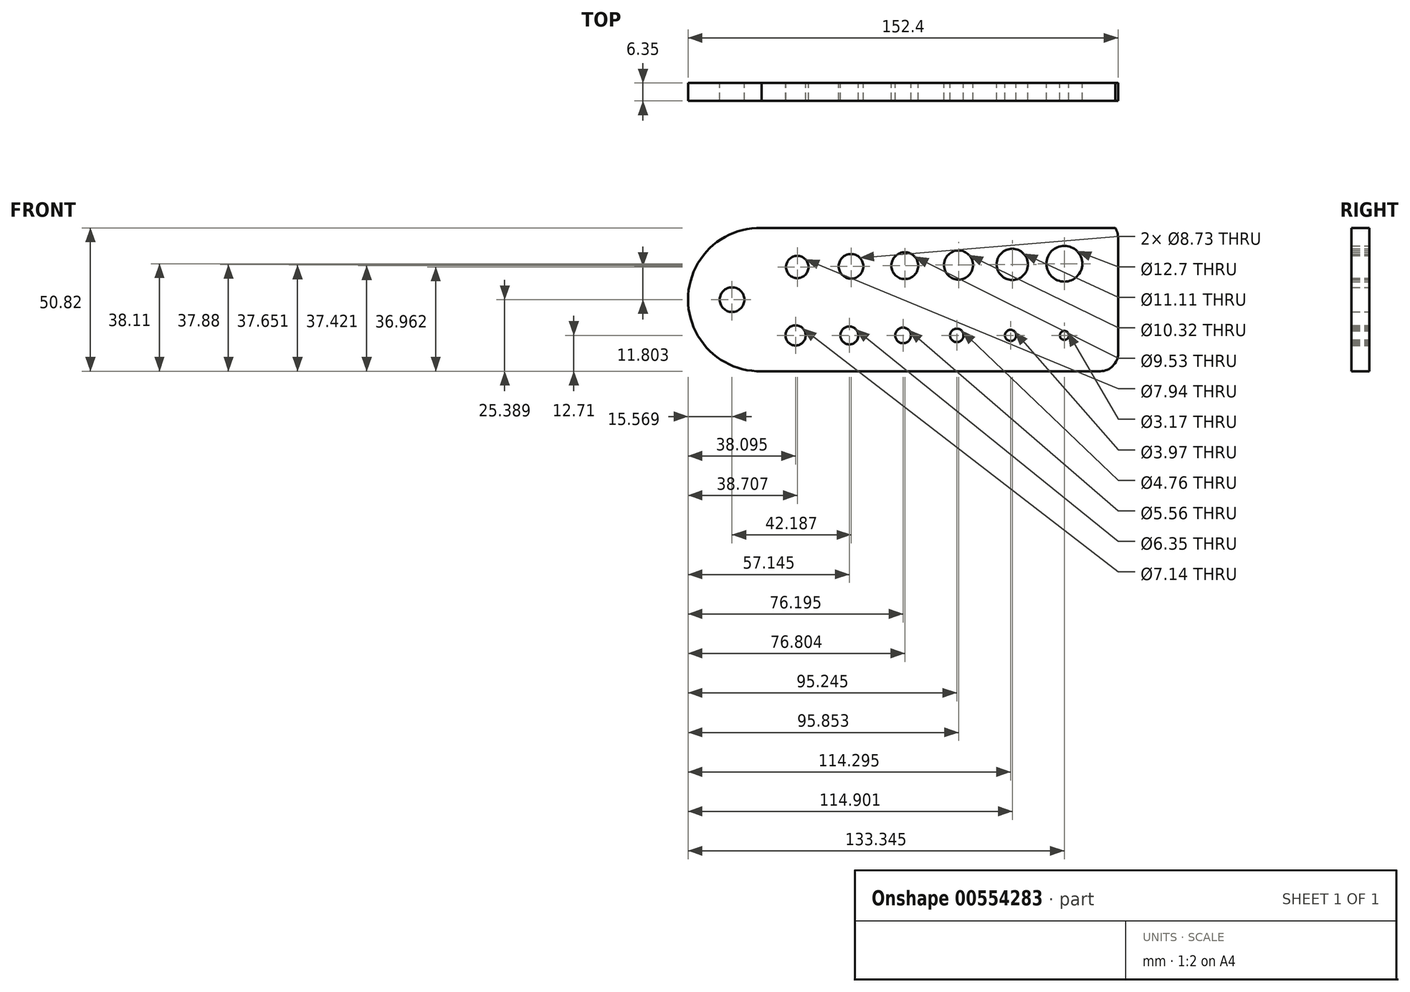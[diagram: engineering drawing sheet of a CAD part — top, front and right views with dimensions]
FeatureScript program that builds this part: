
annotation { "Feature Type Name" : "Feature", "Feature Type Description" : "" }
export const myFeature = defineFeature(function(context is Context, id is Id, definition is map)
    precondition{}
    {
        {
            var Q0;
            Q0=qCreatedBy(makeId("Front.planeOp"),FACE);
            var sketch = newSketch(context, id + "F0", { "sketchPlane" : qUnion([Q0])});
            skLineSegment(sketch, "E0.bottom", {"start": v(0, 0) * mm, "end": v(120.05, 0) * mm});
            skLineSegment(sketch, "E0.top", {"start": v(0, 50.8) * mm, "end": v(125.41, 50.8) * mm});
            skLineSegment(sketch, "E0.right", {"start": v(126.4, 6.35) * mm, "end": v(126.4, 47.4) * mm});
            skPoint(sketch, "E1.visualSharp", {"position": v(126.4, 50.8) * mm});
            skArc(sketch, "E1.filletArc", {"start": v(126.4, 47.4) * mm, "mid": v(126.14, 49.17) * mm, "end": v(125.41, 50.8) * mm});
            skPoint(sketch, "E2.visualSharp", {"position": v(126.4, 0) * mm});
            skArc(sketch, "E2.filletArc", {"start": v(120.05, 0) * mm, "mid": v(124.54, 1.86) * mm, "end": v(126.4, 6.35) * mm});
            skArc(sketch, "E3", {"start": v(0, 50.8) * mm, "mid": v(-26, 25.4) * mm, "end": v(0, 0) * mm});
            skCircle(sketch, "E4", {"center": v(107.35, 38.1) * mm, "radius": 6.35 * mm});
            skCircle(sketch, "E5.1.0.0", {"center": v(88.9, 37.87) * mm, "radius": 5.56 * mm});
            skCircle(sketch, "E5.2.0.0", {"center": v(69.85, 37.64) * mm, "radius": 5.16 * mm});
            skCircle(sketch, "E5.3.0.0", {"center": v(50.8, 37.41) * mm, "radius": 4.76 * mm});
            skCircle(sketch, "E5.4.0.0", {"center": v(31.76, 37.18) * mm, "radius": 4.37 * mm});
            skCircle(sketch, "E5.5.0.0", {"center": v(12.7, 36.95) * mm, "radius": 3.97 * mm});
            skLineSegment(sketch, "E5.direction1", {"start": v(107.95, 38.1) * mm, "end": v(88.9, 37.87) * mm, "construction": true});
            skCircle(sketch, "E6", {"center": v(107.35, 12.7) * mm, "radius": 1.59 * mm});
            skCircle(sketch, "E7.1.0.0", {"center": v(88.3, 12.7) * mm, "radius": 1.98 * mm});
            skCircle(sketch, "E7.2.0.0", {"center": v(69.25, 12.7) * mm, "radius": 2.38 * mm});
            skCircle(sketch, "E7.3.0.0", {"center": v(50.2, 12.7) * mm, "radius": 2.78 * mm});
            skCircle(sketch, "E7.4.0.0", {"center": v(31.15, 12.7) * mm, "radius": 3.18 * mm});
            skCircle(sketch, "E7.5.0.0", {"center": v(12.1, 12.7) * mm, "radius": 3.57 * mm});
            skLineSegment(sketch, "E7.direction1", {"start": v(107.35, 12.7) * mm, "end": v(88.3, 12.7) * mm, "construction": true});
            skCircle(sketch, "E8", {"center": v(-10.43, 25.38) * mm, "radius": 4.37 * mm});
            skSolve(sketch);
        }
        {
            var Q0;
            Q0 = qSketchRegion(id + "F0", true);
            extrude(context, id + "F1", {"entities" : qUnion([Q0]), "depth" : 6.35 * mm, "offsetDistance" : 25.4 * mm});
        }
    });
